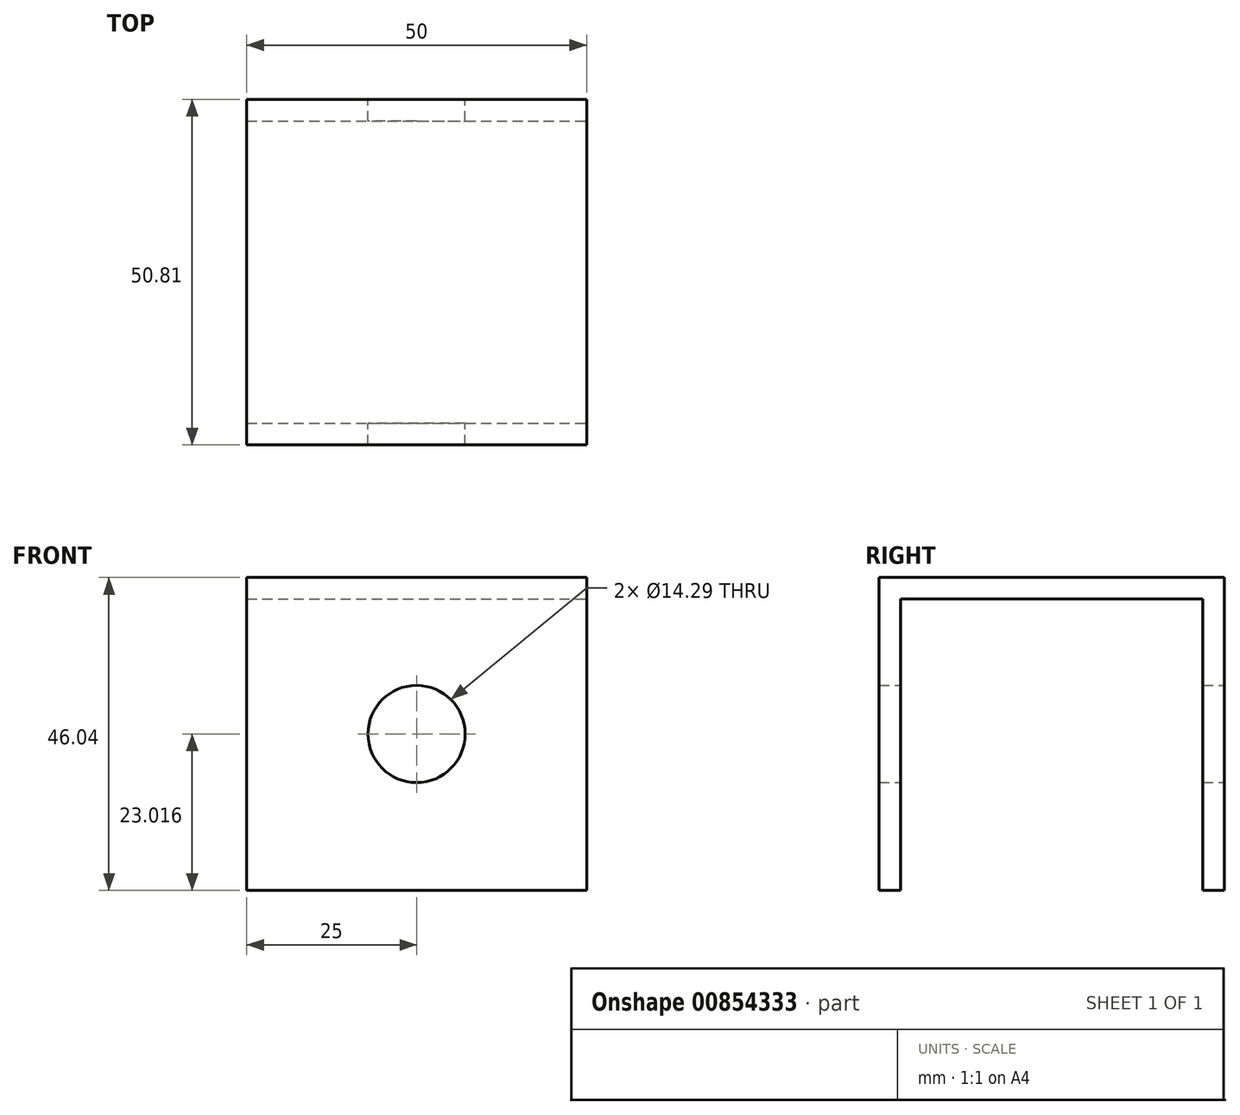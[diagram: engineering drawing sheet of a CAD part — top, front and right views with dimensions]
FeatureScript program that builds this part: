
annotation { "Feature Type Name" : "Feature", "Feature Type Description" : "" }
export const myFeature = defineFeature(function(context is Context, id is Id, definition is map)
    precondition{}
    {
        {
            var Q0;
            Q0=qCreatedBy(makeId("Right.planeOp"),FACE);
            var sketch = newSketch(context, id + "F0", { "sketchPlane" : qUnion([Q0])});
            skLineSegment(sketch, "E0.bottom", {"start": v(0, 0) * mm, "end": v(44.45, 0) * mm});
            skLineSegment(sketch, "E0.left", {"start": v(0, 0) * mm, "end": v(0, -42.86) * mm});
            skLineSegment(sketch, "E0.right", {"start": v(44.45, 0) * mm, "end": v(44.45, -42.86) * mm});
            skLineSegment(sketch, "E1.0", {"start": v(-3.18, 3.17) * mm, "end": v(-3.17, -42.86) * mm});
            skLineSegment(sketch, "E1.1", {"start": v(-3.17, 3.18) * mm, "end": v(47.62, 3.18) * mm});
            skLineSegment(sketch, "E1.2", {"start": v(47.62, 3.17) * mm, "end": v(47.62, -42.86) * mm});
            skLineSegment(sketch, "E2", {"start": v(0, -42.86) * mm, "end": v(-3.17, -42.86) * mm});
            skLineSegment(sketch, "E3", {"start": v(44.45, -42.86) * mm, "end": v(47.62, -42.86) * mm});
            skSolve(sketch);
        }
        {
            var Q0;
            Q0=makeQuery(id+"F0.imprint","IMPRINT",FACE,{"disambiguationData":[TD([[makeQuery(id+"F0.imprint","IMPRINT",EDGE,{"derivedFrom":sQuery(id+"F0.wireOp",EDGE,"E0.bottom")}),1.0]])]});
            extrude(context, id + "F1", {"entities" : qUnion([Q0]), "oppositeDirection" : true, "depth" : 50 * mm, "offsetDistance" : 25 * mm});
        }
        {
            var Q0;
            Q0=makeQuery(id+"F1.opExtrude","SWEPT_FACE",FACE,{"disambiguationData":[OSD([sQuery(id+"F0.wireOp",EDGE,"E1.2")])]});
            var sketch = newSketch(context, id + "F2", { "sketchPlane" : qUnion([Q0])});
            skCircle(sketch, "E4", {"center": v(25, -19.84) * mm, "radius": 7.14 * mm});
            skLineSegment(sketch, "E5", {"start": v(50, -19.84) * mm, "end": v(0, -19.84) * mm, "construction": true});
            skLineSegment(sketch, "E6", {"start": v(25, 3.17) * mm, "end": v(25, -42.86) * mm, "construction": true});
            skSolve(sketch);
        }
        {
            var Q0;
            Q0=qSketchRegion(id+"F2",true);
            extrude(context, id + "F3", {"entities" : qUnion([Q0]), "operationType" : NewBodyOperationType.REMOVE, "endBound" : BoundingType.THROUGH_ALL, "oppositeDirection" : true, "depth" : 25 * mm, "offsetDistance" : 25 * mm});
        }
    });
